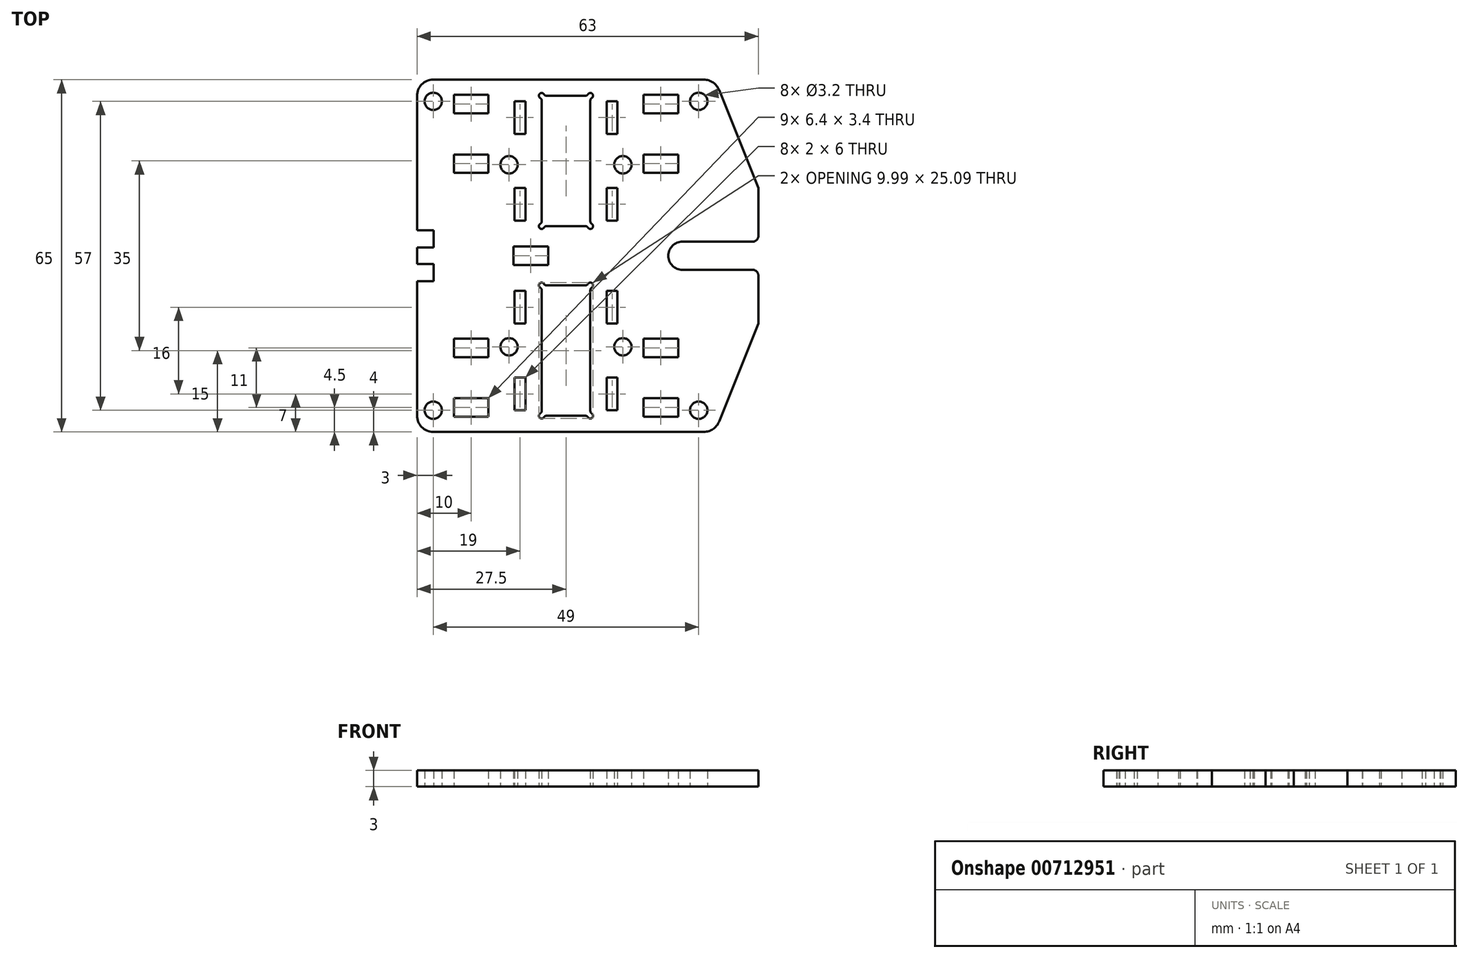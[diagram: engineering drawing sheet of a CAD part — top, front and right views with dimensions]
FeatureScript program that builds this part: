
annotation { "Feature Type Name" : "Feature", "Feature Type Description" : "" }
export const myFeature = defineFeature(function(context is Context, id is Id, definition is map)
    precondition{}
    {
        {
            var Q0;
            Q0=qCreatedBy(makeId("Top.planeOp"),FACE);
            var sketch = newSketch(context, id + "F0", { "sketchPlane" : qUnion([Q0])});
            skLineSegment(sketch, "E0", {"start": v(-31.5, -1.5) * mm, "end": v(-31.5, 1.5) * mm});
            skArc(sketch, "E1", {"start": v(-8.75, -29.12) * mm, "mid": v(-8.85, -29.9) * mm, "end": v(-8.07, -29.8) * mm});
            skArc(sketch, "E2", {"start": v(-7.63, -29.55) * mm, "mid": v(-7.88, -29.62) * mm, "end": v(-8.07, -29.8) * mm});
            skArc(sketch, "E3", {"start": v(-8.75, -29.12) * mm, "mid": v(-8.57, -28.93) * mm, "end": v(-8.5, -28.68) * mm});
            skLineSegment(sketch, "E4", {"start": v(-8.5, -6.32) * mm, "end": v(-8.5, -28.68) * mm});
            skArc(sketch, "E5", {"start": v(-8.5, -6.32) * mm, "mid": v(-8.57, -6.07) * mm, "end": v(-8.75, -5.88) * mm});
            skArc(sketch, "E6", {"start": v(-8.07, -5.2) * mm, "mid": v(-8.85, -5.1) * mm, "end": v(-8.75, -5.88) * mm});
            skArc(sketch, "E7", {"start": v(-8.07, -5.2) * mm, "mid": v(-7.88, -5.38) * mm, "end": v(-7.63, -5.45) * mm});
            skLineSegment(sketch, "E8", {"start": v(-0.37, -5.45) * mm, "end": v(-7.63, -5.45) * mm});
            skArc(sketch, "E9", {"start": v(-0.37, -5.45) * mm, "mid": v(-0.12, -5.38) * mm, "end": v(0.07, -5.2) * mm});
            skArc(sketch, "E10", {"start": v(0.75, -5.88) * mm, "mid": v(0.85, -5.1) * mm, "end": v(0.07, -5.2) * mm});
            skArc(sketch, "E11", {"start": v(0.75, -5.88) * mm, "mid": v(0.57, -6.07) * mm, "end": v(0.5, -6.32) * mm});
            skLineSegment(sketch, "E12", {"start": v(0.5, -28.68) * mm, "end": v(0.5, -6.32) * mm});
            skArc(sketch, "E13", {"start": v(0.5, -28.68) * mm, "mid": v(0.57, -28.93) * mm, "end": v(0.75, -29.12) * mm});
            skArc(sketch, "E14", {"start": v(0.07, -29.8) * mm, "mid": v(0.85, -29.9) * mm, "end": v(0.75, -29.12) * mm});
            skArc(sketch, "E15", {"start": v(0.07, -29.8) * mm, "mid": v(-0.12, -29.62) * mm, "end": v(-0.37, -29.55) * mm});
            skLineSegment(sketch, "E16", {"start": v(-7.63, -29.55) * mm, "end": v(-0.37, -29.55) * mm});
            skArc(sketch, "E17", {"start": v(-8.75, 5.88) * mm, "mid": v(-8.85, 5.1) * mm, "end": v(-8.07, 5.2) * mm});
            skArc(sketch, "E18", {"start": v(-7.63, 5.45) * mm, "mid": v(-7.88, 5.38) * mm, "end": v(-8.07, 5.2) * mm});
            skArc(sketch, "E19", {"start": v(-8.75, 5.88) * mm, "mid": v(-8.57, 6.07) * mm, "end": v(-8.5, 6.32) * mm});
            skLineSegment(sketch, "E20", {"start": v(-8.5, 28.68) * mm, "end": v(-8.5, 6.32) * mm});
            skArc(sketch, "E21", {"start": v(-8.5, 28.68) * mm, "mid": v(-8.57, 28.93) * mm, "end": v(-8.75, 29.12) * mm});
            skArc(sketch, "E22", {"start": v(-8.07, 29.8) * mm, "mid": v(-8.85, 29.9) * mm, "end": v(-8.75, 29.12) * mm});
            skArc(sketch, "E23", {"start": v(-8.07, 29.8) * mm, "mid": v(-7.88, 29.62) * mm, "end": v(-7.63, 29.55) * mm});
            skLineSegment(sketch, "E24", {"start": v(-0.37, 29.55) * mm, "end": v(-7.63, 29.55) * mm});
            skArc(sketch, "E25", {"start": v(-0.37, 29.55) * mm, "mid": v(-0.12, 29.62) * mm, "end": v(0.07, 29.8) * mm});
            skArc(sketch, "E26", {"start": v(0.75, 29.12) * mm, "mid": v(0.85, 29.9) * mm, "end": v(0.07, 29.8) * mm});
            skArc(sketch, "E27", {"start": v(0.75, 29.12) * mm, "mid": v(0.57, 28.93) * mm, "end": v(0.5, 28.68) * mm});
            skLineSegment(sketch, "E28", {"start": v(0.5, 6.32) * mm, "end": v(0.5, 28.68) * mm});
            skArc(sketch, "E29", {"start": v(0.5, 6.32) * mm, "mid": v(0.57, 6.07) * mm, "end": v(0.75, 5.88) * mm});
            skArc(sketch, "E30", {"start": v(0.07, 5.2) * mm, "mid": v(0.85, 5.1) * mm, "end": v(0.75, 5.88) * mm});
            skArc(sketch, "E31", {"start": v(0.07, 5.2) * mm, "mid": v(-0.12, 5.38) * mm, "end": v(-0.37, 5.45) * mm});
            skLineSegment(sketch, "E32", {"start": v(-7.63, 5.45) * mm, "end": v(-0.37, 5.45) * mm});
            skLineSegment(sketch, "E33", {"start": v(-31.5, -4.7) * mm, "end": v(-28.4, -4.7) * mm});
            skLineSegment(sketch, "E34", {"start": v(-28.4, -1.5) * mm, "end": v(-31.5, -1.5) * mm});
            skLineSegment(sketch, "E35", {"start": v(-28.4, -4.7) * mm, "end": v(-28.4, -1.5) * mm});
            skLineSegment(sketch, "E36", {"start": v(-31.5, 1.5) * mm, "end": v(-28.4, 1.5) * mm});
            skLineSegment(sketch, "E37", {"start": v(-28.4, 4.7) * mm, "end": v(-31.5, 4.7) * mm});
            skLineSegment(sketch, "E38", {"start": v(-28.4, 1.5) * mm, "end": v(-28.4, 4.7) * mm});
            skLineSegment(sketch, "E39", {"start": v(-13.7, 1.7) * mm, "end": v(-13.7, -1.7) * mm});
            skLineSegment(sketch, "E40", {"start": v(-13.7, -1.7) * mm, "end": v(-7.3, -1.7) * mm});
            skLineSegment(sketch, "E41", {"start": v(-13.7, 1.7) * mm, "end": v(-7.3, 1.7) * mm});
            skLineSegment(sketch, "E42", {"start": v(-7.3, -1.7) * mm, "end": v(-7.3, 1.7) * mm});
            skLineSegment(sketch, "E43", {"start": v(3.5, -12.5) * mm, "end": v(5.5, -12.5) * mm});
            skLineSegment(sketch, "E44", {"start": v(-13.5, -12.5) * mm, "end": v(-11.5, -12.5) * mm});
            skLineSegment(sketch, "E45", {"start": v(5.5, 12.5) * mm, "end": v(3.5, 12.5) * mm});
            skLineSegment(sketch, "E46", {"start": v(-11.5, 12.5) * mm, "end": v(-13.5, 12.5) * mm});
            skLineSegment(sketch, "E47", {"start": v(3.5, 22.5) * mm, "end": v(5.5, 22.5) * mm});
            skLineSegment(sketch, "E48", {"start": v(-13.5, 22.5) * mm, "end": v(-11.5, 22.5) * mm});
            skLineSegment(sketch, "E49", {"start": v(5.5, -22.5) * mm, "end": v(3.5, -22.5) * mm});
            skLineSegment(sketch, "E50", {"start": v(-11.5, -22.5) * mm, "end": v(-13.5, -22.5) * mm});
            skLineSegment(sketch, "E51", {"start": v(-13.5, -28.5) * mm, "end": v(-11.5, -28.5) * mm});
            skLineSegment(sketch, "E52", {"start": v(-11.5, -6.5) * mm, "end": v(-13.5, -6.5) * mm});
            skLineSegment(sketch, "E53", {"start": v(-13.5, 6.5) * mm, "end": v(-11.5, 6.5) * mm});
            skLineSegment(sketch, "E54", {"start": v(-11.5, 28.5) * mm, "end": v(-13.5, 28.5) * mm});
            skLineSegment(sketch, "E55", {"start": v(3.5, -28.5) * mm, "end": v(5.5, -28.5) * mm});
            skLineSegment(sketch, "E56", {"start": v(5.5, -6.5) * mm, "end": v(3.5, -6.5) * mm});
            skLineSegment(sketch, "E57", {"start": v(3.5, 6.5) * mm, "end": v(5.5, 6.5) * mm});
            skLineSegment(sketch, "E58", {"start": v(5.5, 28.5) * mm, "end": v(3.5, 28.5) * mm});
            skLineSegment(sketch, "E59", {"start": v(-13.5, -22.5) * mm, "end": v(-13.5, -28.5) * mm});
            skLineSegment(sketch, "E60", {"start": v(-11.5, -28.5) * mm, "end": v(-11.5, -22.5) * mm});
            skLineSegment(sketch, "E61", {"start": v(-13.5, -6.5) * mm, "end": v(-13.5, -12.5) * mm});
            skLineSegment(sketch, "E62", {"start": v(-11.5, -12.5) * mm, "end": v(-11.5, -6.5) * mm});
            skLineSegment(sketch, "E63", {"start": v(-13.5, 12.5) * mm, "end": v(-13.5, 6.5) * mm});
            skLineSegment(sketch, "E64", {"start": v(-11.5, 6.5) * mm, "end": v(-11.5, 12.5) * mm});
            skLineSegment(sketch, "E65", {"start": v(-13.5, 28.5) * mm, "end": v(-13.5, 22.5) * mm});
            skLineSegment(sketch, "E66", {"start": v(-11.5, 22.5) * mm, "end": v(-11.5, 28.5) * mm});
            skLineSegment(sketch, "E67", {"start": v(3.5, -22.5) * mm, "end": v(3.5, -28.5) * mm});
            skLineSegment(sketch, "E68", {"start": v(5.5, -28.5) * mm, "end": v(5.5, -22.5) * mm});
            skLineSegment(sketch, "E69", {"start": v(3.5, -6.5) * mm, "end": v(3.5, -12.5) * mm});
            skLineSegment(sketch, "E70", {"start": v(5.5, -12.5) * mm, "end": v(5.5, -6.5) * mm});
            skLineSegment(sketch, "E71", {"start": v(3.5, 12.5) * mm, "end": v(3.5, 6.5) * mm});
            skLineSegment(sketch, "E72", {"start": v(5.5, 6.5) * mm, "end": v(5.5, 12.5) * mm});
            skLineSegment(sketch, "E73", {"start": v(3.5, 28.5) * mm, "end": v(3.5, 22.5) * mm});
            skLineSegment(sketch, "E74", {"start": v(5.5, 22.5) * mm, "end": v(5.5, 28.5) * mm});
            skArc(sketch, "E75", {"start": v(17.5, 2.6) * mm, "mid": v(14.9, 0) * mm, "end": v(17.5, -2.6) * mm});
            skLineSegment(sketch, "E76", {"start": v(31.5, 12.5) * mm, "end": v(31.5, 3.6) * mm});
            skLineSegment(sketch, "E77", {"start": v(17.5, 2.6) * mm, "end": v(30.5, 2.6) * mm});
            skArc(sketch, "E78", {"start": v(30.5, 2.6) * mm, "mid": v(31.2, 2.9) * mm, "end": v(31.5, 3.6) * mm});
            skLineSegment(sketch, "E79", {"start": v(17.5, -2.6) * mm, "end": v(30.5, -2.6) * mm});
            skLineSegment(sketch, "E80", {"start": v(31.5, -12.5) * mm, "end": v(31.5, -3.6) * mm});
            skArc(sketch, "E81", {"start": v(31.5, -3.6) * mm, "mid": v(31.2, -2.9) * mm, "end": v(30.5, -2.6) * mm});
            skLineSegment(sketch, "E82", {"start": v(10.3, -26.3) * mm, "end": v(10.3, -29.7) * mm});
            skLineSegment(sketch, "E83", {"start": v(10.3, -29.7) * mm, "end": v(16.7, -29.7) * mm});
            skLineSegment(sketch, "E84", {"start": v(10.3, -26.3) * mm, "end": v(16.7, -26.3) * mm});
            skLineSegment(sketch, "E85", {"start": v(16.7, -29.7) * mm, "end": v(16.7, -26.3) * mm});
            skLineSegment(sketch, "E86", {"start": v(10.3, -15.3) * mm, "end": v(10.3, -18.7) * mm});
            skLineSegment(sketch, "E87", {"start": v(10.3, -18.7) * mm, "end": v(16.7, -18.7) * mm});
            skLineSegment(sketch, "E88", {"start": v(10.3, -15.3) * mm, "end": v(16.7, -15.3) * mm});
            skLineSegment(sketch, "E89", {"start": v(16.7, -18.7) * mm, "end": v(16.7, -15.3) * mm});
            skLineSegment(sketch, "E90", {"start": v(10.3, 18.7) * mm, "end": v(10.3, 15.3) * mm});
            skLineSegment(sketch, "E91", {"start": v(10.3, 15.3) * mm, "end": v(16.7, 15.3) * mm});
            skLineSegment(sketch, "E92", {"start": v(10.3, 18.7) * mm, "end": v(16.7, 18.7) * mm});
            skLineSegment(sketch, "E93", {"start": v(16.7, 15.3) * mm, "end": v(16.7, 18.7) * mm});
            skLineSegment(sketch, "E94", {"start": v(10.3, 29.7) * mm, "end": v(10.3, 26.3) * mm});
            skLineSegment(sketch, "E95", {"start": v(10.3, 26.3) * mm, "end": v(16.7, 26.3) * mm});
            skLineSegment(sketch, "E96", {"start": v(10.3, 29.7) * mm, "end": v(16.7, 29.7) * mm});
            skLineSegment(sketch, "E97", {"start": v(16.7, 26.3) * mm, "end": v(16.7, 29.7) * mm});
            skCircle(sketch, "E98", {"center": v(20.5, -28.5) * mm, "radius": 1.6 * mm});
            skCircle(sketch, "E99", {"center": v(20.5, 28.5) * mm, "radius": 1.6 * mm});
            skLineSegment(sketch, "E100", {"start": v(-24.7, -26.3) * mm, "end": v(-24.7, -29.7) * mm});
            skLineSegment(sketch, "E101", {"start": v(-24.7, -29.7) * mm, "end": v(-18.3, -29.7) * mm});
            skLineSegment(sketch, "E102", {"start": v(-24.7, -26.3) * mm, "end": v(-18.3, -26.3) * mm});
            skLineSegment(sketch, "E103", {"start": v(-18.3, -29.7) * mm, "end": v(-18.3, -26.3) * mm});
            skLineSegment(sketch, "E104", {"start": v(-24.7, -15.3) * mm, "end": v(-24.7, -18.7) * mm});
            skLineSegment(sketch, "E105", {"start": v(-24.7, -18.7) * mm, "end": v(-18.3, -18.7) * mm});
            skLineSegment(sketch, "E106", {"start": v(-24.7, -15.3) * mm, "end": v(-18.3, -15.3) * mm});
            skLineSegment(sketch, "E107", {"start": v(-18.3, -18.7) * mm, "end": v(-18.3, -15.3) * mm});
            skLineSegment(sketch, "E108", {"start": v(-24.7, 18.7) * mm, "end": v(-24.7, 15.3) * mm});
            skLineSegment(sketch, "E109", {"start": v(-24.7, 15.3) * mm, "end": v(-18.3, 15.3) * mm});
            skLineSegment(sketch, "E110", {"start": v(-24.7, 18.7) * mm, "end": v(-18.3, 18.7) * mm});
            skLineSegment(sketch, "E111", {"start": v(-18.3, 15.3) * mm, "end": v(-18.3, 18.7) * mm});
            skLineSegment(sketch, "E112", {"start": v(-24.7, 29.7) * mm, "end": v(-24.7, 26.3) * mm});
            skLineSegment(sketch, "E113", {"start": v(-24.7, 26.3) * mm, "end": v(-18.3, 26.3) * mm});
            skLineSegment(sketch, "E114", {"start": v(-24.7, 29.7) * mm, "end": v(-18.3, 29.7) * mm});
            skLineSegment(sketch, "E115", {"start": v(-18.3, 26.3) * mm, "end": v(-18.3, 29.7) * mm});
            skCircle(sketch, "E116", {"center": v(-28.5, -28.5) * mm, "radius": 1.6 * mm});
            skCircle(sketch, "E117", {"center": v(-28.5, 28.5) * mm, "radius": 1.6 * mm});
            skCircle(sketch, "E118", {"center": v(-14.5, -16.8) * mm, "radius": 1.6 * mm});
            skCircle(sketch, "E119", {"center": v(6.5, -16.8) * mm, "radius": 1.6 * mm});
            skCircle(sketch, "E120", {"center": v(6.5, 16.8) * mm, "radius": 1.6 * mm});
            skCircle(sketch, "E121", {"center": v(-14.5, 16.8) * mm, "radius": 1.6 * mm});
            skArc(sketch, "E122", {"start": v(24.25, 30.61) * mm, "mid": v(23.15, 31.98) * mm, "end": v(21.47, 32.5) * mm});
            skLineSegment(sketch, "E123", {"start": v(31.5, -12.5) * mm, "end": v(24.25, -30.61) * mm});
            skArc(sketch, "E124", {"start": v(21.47, -32.5) * mm, "mid": v(23.15, -31.98) * mm, "end": v(24.25, -30.61) * mm});
            skLineSegment(sketch, "E125", {"start": v(-31.5, -29.5) * mm, "end": v(-31.5, -4.7) * mm});
            skLineSegment(sketch, "E126", {"start": v(21.47, -32.5) * mm, "end": v(-28.5, -32.5) * mm});
            skArc(sketch, "E127", {"start": v(-31.5, -29.5) * mm, "mid": v(-30.62, -31.62) * mm, "end": v(-28.5, -32.5) * mm});
            skLineSegment(sketch, "E128", {"start": v(-31.5, 4.7) * mm, "end": v(-31.5, 29.5) * mm});
            skLineSegment(sketch, "E129", {"start": v(21.47, 32.5) * mm, "end": v(-28.5, 32.5) * mm});
            skArc(sketch, "E130", {"start": v(-28.5, 32.5) * mm, "mid": v(-30.62, 31.62) * mm, "end": v(-31.5, 29.5) * mm});
            skLineSegment(sketch, "E131", {"start": v(24.25, 30.61) * mm, "end": v(31.5, 12.5) * mm});
            skSolve(sketch);
        }
        {
            var Q0;
            Q0=qSketchRegion(id+"F0",true);
            extrude(context, id + "F1", {"entities" : qUnion([Q0]), "depth" : 3 * mm, "offsetDistance" : 25 * mm});
        }
        {
            var Q0;
            Q0=makeQuery(id+"F1.opExtrude","CAP_EDGE",EDGE,{"disambiguationData":[OSD([sQuery(id+"F0.wireOp",EDGE,"E20")])],"isStart":false});
            cPoint(context, id + "F2", {"entities" : qUnion([Q0]), "parameter" : 0.5});
        }
        {
            var Q0;
            Q0 = qCreatedBy(id + "F2" ,VERTEX);
            var Q1;
            Q1=makeQuery(id+"F1.opExtrude","CAP_EDGE",EDGE,{"disambiguationData":[OSD([sQuery(id+"F0.wireOp",EDGE,"E20")])],"isStart":false});
            cPlane(context, id + "F3", {"entities" : qUnion([Q0, Q1]), "cplaneType" : CPlaneType.LINE_POINT, "offset" : 25 * mm, "width" : 150 * mm, "height" : 150 * mm});
        }
        {
            var Q0;
            Q0=qCreatedBy(id+"F3.planeOp",FACE);
            var sketch = newSketch(context, id + "F4", { "sketchPlane" : qUnion([Q0])});
            skCircle(sketch, "E132", {"center": v(-4, 9) * mm, "radius": 7.5 * mm, "construction": true});
            skSolve(sketch);
        }
        {
            var Q0;
            Q0=makeQuery(id+"F1.opExtrude","CAP_EDGE",EDGE,{"disambiguationData":[OSD([sQuery(id+"F0.wireOp",EDGE,"E12")])],"isStart":false});
            cPoint(context, id + "F5", {"entities" : qUnion([Q0]), "parameter" : 0.5});
        }
        {
            var Q0;
            Q0 = qCreatedBy(id + "F5" ,VERTEX);
            var Q1;
            Q1=makeQuery(id+"F1.opExtrude","CAP_EDGE",EDGE,{"disambiguationData":[OSD([sQuery(id+"F0.wireOp",EDGE,"E12")])],"isStart":false});
            cPlane(context, id + "F6", {"entities" : qUnion([Q0, Q1]), "cplaneType" : CPlaneType.LINE_POINT, "offset" : 25 * mm, "width" : 150 * mm, "height" : 150 * mm});
        }
        {
            var Q0;
            Q0=qCreatedBy(id+"F6.planeOp",FACE);
            var sketch = newSketch(context, id + "F7", { "sketchPlane" : qUnion([Q0])});
            skCircle(sketch, "E133.0", {"center": v(4, 9) * mm, "radius": 7.5 * mm, "construction": true});
            skSolve(sketch);
        }
    });
